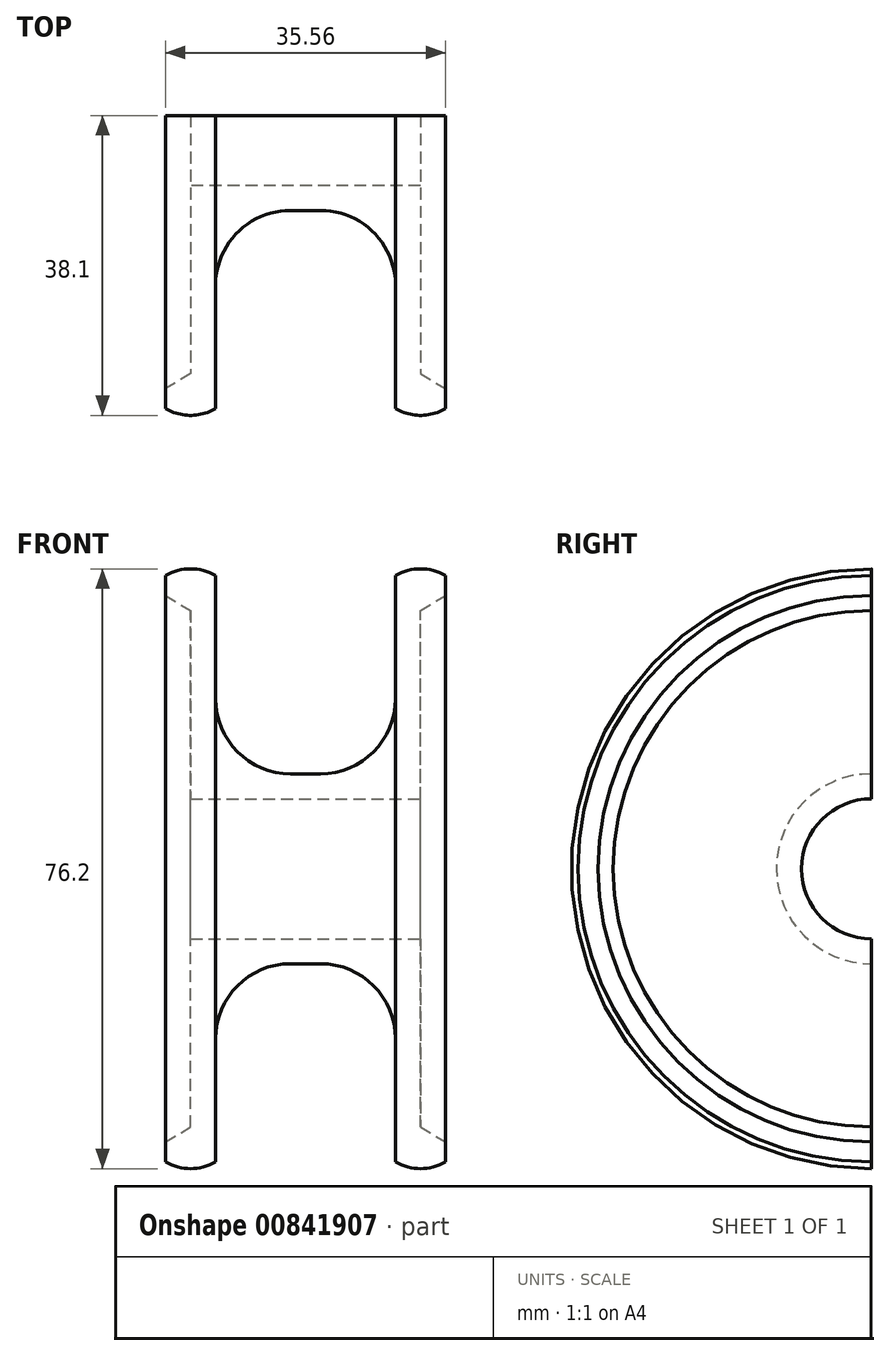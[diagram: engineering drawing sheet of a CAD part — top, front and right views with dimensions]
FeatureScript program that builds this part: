
annotation { "Feature Type Name" : "Feature", "Feature Type Description" : "" }
export const myFeature = defineFeature(function(context is Context, id is Id, definition is map)
    precondition{}
    {
        {
            var Q0;
            Q0=qCreatedBy(makeId("Top.planeOp"),FACE);
            var sketch = newSketch(context, id + "F0", { "sketchPlane" : qUnion([Q0])});
            skLineSegment(sketch, "E0", {"start": v(-11.43, -37.25) * mm, "end": v(-11.43, -12.06) * mm});
            skLineSegment(sketch, "E1", {"start": v(-11.43, -12.06) * mm, "end": v(11.43, -12.06) * mm});
            skLineSegment(sketch, "E2", {"start": v(11.43, -12.06) * mm, "end": v(11.43, -37.25) * mm});
            skLineSegment(sketch, "E3.0", {"start": v(14.6, -32.8) * mm, "end": v(17.78, -34.7) * mm});
            skLineSegment(sketch, "E3.1", {"start": v(-17.78, -34.7) * mm, "end": v(-14.6, -32.8) * mm});
            skLineSegment(sketch, "E3.2", {"start": v(-14.6, -32.8) * mm, "end": v(-14.6, -8.89) * mm});
            skLineSegment(sketch, "E3.3", {"start": v(-14.6, -8.89) * mm, "end": v(14.6, -8.89) * mm});
            skLineSegment(sketch, "E3.4", {"start": v(14.6, -8.89) * mm, "end": v(14.6, -32.8) * mm});
            skLineSegment(sketch, "E4", {"start": v(-17.78, -37.25) * mm, "end": v(-17.78, -34.7) * mm});
            skLineSegment(sketch, "E5", {"start": v(17.78, -37.25) * mm, "end": v(17.78, -34.7) * mm});
            skArc(sketch, "E6", {"start": v(-17.78, -37.25) * mm, "mid": v(-14.6, -38.1) * mm, "end": v(-11.43, -37.25) * mm});
            skArc(sketch, "E7", {"start": v(11.43, -37.25) * mm, "mid": v(14.6, -38.1) * mm, "end": v(17.78, -37.25) * mm});
            skLineSegment(sketch, "E8", {"start": v(-14.6, 0) * mm, "end": v(14.6, 0) * mm, "construction": true});
            skPoint(sketch, "E8.endSnap0", {"position": v(14.6, -20.85) * mm});
            skLineSegment(sketch, "E9", {"start": v(0, -8.89) * mm, "end": v(0, -12.06) * mm, "construction": true});
            skPoint(sketch, "E10", {"position": v(-14.6, -38.1) * mm});
            skSolve(sketch);
        }
        {
            var Q0;
            Q0 = qSketchRegion(id + "F0", true);
            var Q1;
            Q1=sQuery(id+"F0.wireOp",EDGE,"E8");
            revolve(context, id + "F1", {"surfaceOperationType" : NewSurfaceOperationType.NEW, "entities" : qUnion([Q0]), "axis" : qUnion([Q1]), "revolveType" : RevolveType.SYMMETRIC, "angle" : 180 * degree});
        }
        {
            var Q0;
            Q0=makeQuery(id+"F1.opRevolve","SWEPT_EDGE",EDGE,{"disambiguationData":[OSD([sQuery(id+"F0.wireOp",EDGE,"E1"),sQuery(id+"F0.wireOp",EDGE,"E2")])]});
            var Q1;
            Q1=makeQuery(id+"F1.opRevolve","SWEPT_EDGE",EDGE,{"disambiguationData":[OSD([sQuery(id+"F0.wireOp",EDGE,"E0"),sQuery(id+"F0.wireOp",EDGE,"E1")])]});
            fillet(context, id + "F2", {"entities" : qUnion([Q0, Q1]), "radius" : 9.52 * mm, "tangentPropagation" : true, "allowEdgeOverflow" : false});
        }
    });
